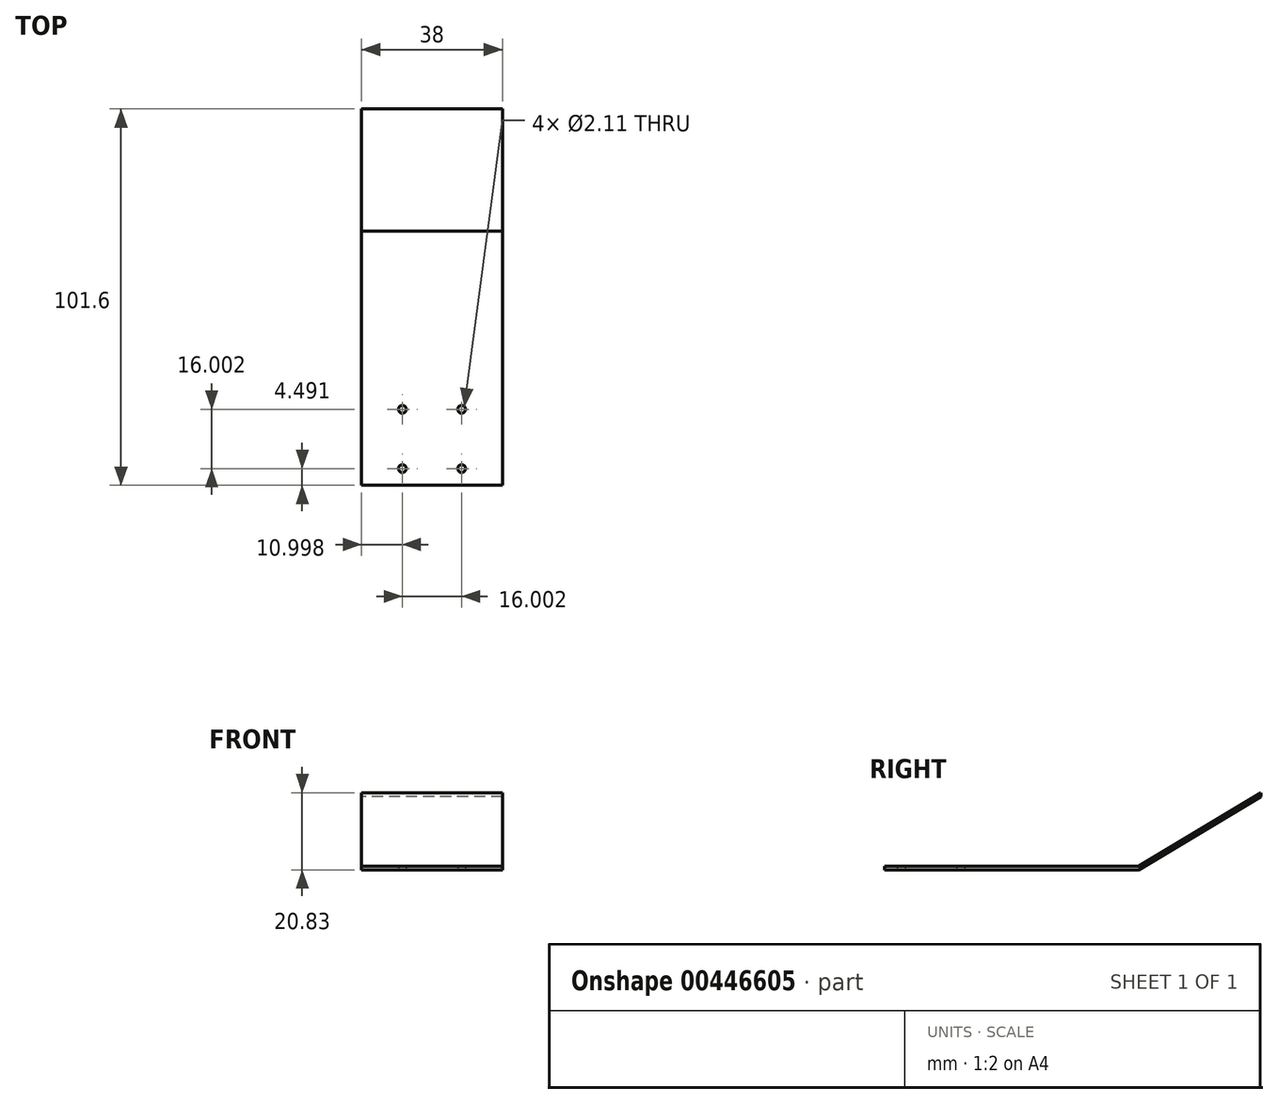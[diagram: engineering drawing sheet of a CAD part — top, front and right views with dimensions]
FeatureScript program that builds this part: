
annotation { "Feature Type Name" : "Feature", "Feature Type Description" : "" }
export const myFeature = defineFeature(function(context is Context, id is Id, definition is map)
    precondition{}
    {
        {
            var Q0;
            Q0=qCreatedBy(makeId("Right.planeOp"),FACE);
            var sketch = newSketch(context, id + "F0", { "sketchPlane" : qUnion([Q0])});
            skPoint(sketch, "E0.endSnap0", {"position": v(32.28, 66.8) * mm});
            skLineSegment(sketch, "E1", {"start": v(-12.17, 43.31) * mm, "end": v(56.4, 43.31) * mm});
            skLineSegment(sketch, "E2", {"start": v(56.4, 43.31) * mm, "end": v(89.43, 63.13) * mm});
            skLineSegment(sketch, "E3", {"start": v(56.4, 42.3) * mm, "end": v(89.43, 62.12) * mm});
            skLineSegment(sketch, "E4", {"start": v(56.4, 42.3) * mm, "end": v(-12.17, 42.3) * mm});
            skLineSegment(sketch, "E5", {"start": v(89.43, 63.13) * mm, "end": v(89.43, 62.12) * mm});
            skLineSegment(sketch, "E6", {"start": v(-12.17, 43.31) * mm, "end": v(-12.17, 42.3) * mm});
            skSolve(sketch);
        }
        {
            var Q0;
            Q0=makeQuery(id+"F0.imprint","IMPRINT",FACE,{"disambiguationData":[TD([[makeQuery(id+"F0.imprint","IMPRINT",EDGE,{"derivedFrom":sQuery(id+"F0.wireOp",EDGE,"E1")}),-1.0]])]});
            extrude(context, id + "F1", {"entities" : qUnion([Q0]), "depth" : 38 * mm});
        }
        {
            var Q0;
            Q0=makeQuery(id+"F1.opExtrude","SWEPT_FACE",FACE,{"disambiguationData":[OSD([sQuery(id+"F0.wireOp",EDGE,"E4")])]});
            var sketch = newSketch(context, id + "F2", { "sketchPlane" : qUnion([Q0])});
            skCircle(sketch, "E7", {"center": v(27, -8.32) * mm, "radius": 1.05 * mm});
            skCircle(sketch, "E8", {"center": v(27, 7.68) * mm, "radius": 1.05 * mm});
            skCircle(sketch, "E9", {"center": v(11, -8.32) * mm, "radius": 1.05 * mm});
            skCircle(sketch, "E10", {"center": v(11, 7.68) * mm, "radius": 1.05 * mm});
            skLineSegment(sketch, "E11", {"start": v(38, -12.82) * mm, "end": v(0, -12.82) * mm});
            skLineSegment(sketch, "E12", {"start": v(19, 12.17) * mm, "end": v(19, -12.82) * mm});
            skLineSegment(sketch, "E13", {"start": v(38, 12.17) * mm, "end": v(0, -12.82) * mm});
            skLineSegment(sketch, "E14", {"start": v(19, -0.32) * mm, "end": v(0, -0.32) * mm});
            skLineSegment(sketch, "E15", {"start": v(0, -0.32) * mm, "end": v(38, -0.32) * mm});
            skSolve(sketch);
        }
        {
            var Q0;
            Q0=sQuery(id+"F2.wireOp",VERTEX,"E7.center");
            var Q1;
            Q1=sQuery(id+"F2.wireOp",VERTEX,"E9.center");
            var Q2;
            Q2=sQuery(id+"F2.wireOp",VERTEX,"E10.center");
            var Q3;
            Q3=sQuery(id+"F2.wireOp",VERTEX,"E8.center");
            var Q4;
            Q4=makeQuery(id+"F1.opExtrude","SWEPT_BODY",BODY,{"disambiguationData":[OSD([sQuery(id+"F0.wireOp",EDGE,"E1"),sQuery(id+"F0.wireOp",EDGE,"E2"),sQuery(id+"F0.wireOp",EDGE,"E3"),sQuery(id+"F0.wireOp",EDGE,"E4"),sQuery(id+"F0.wireOp",EDGE,"E5"),sQuery(id+"F0.wireOp",EDGE,"E6")])]});
            hole(context, id + "F3", {"style" : HoleStyle.SIMPLE, "endStyle" : HoleEndStyle.THROUGH, "holeDiameter" : 2.1 * mm, "isTappedThrough" : true, "tappedDepth" : 12.7 * mm, "tapClearance" : 3, "locations" : qUnion([Q0, Q1, Q2, Q3]), "scope" : qUnion([Q4])});
        }
    });
